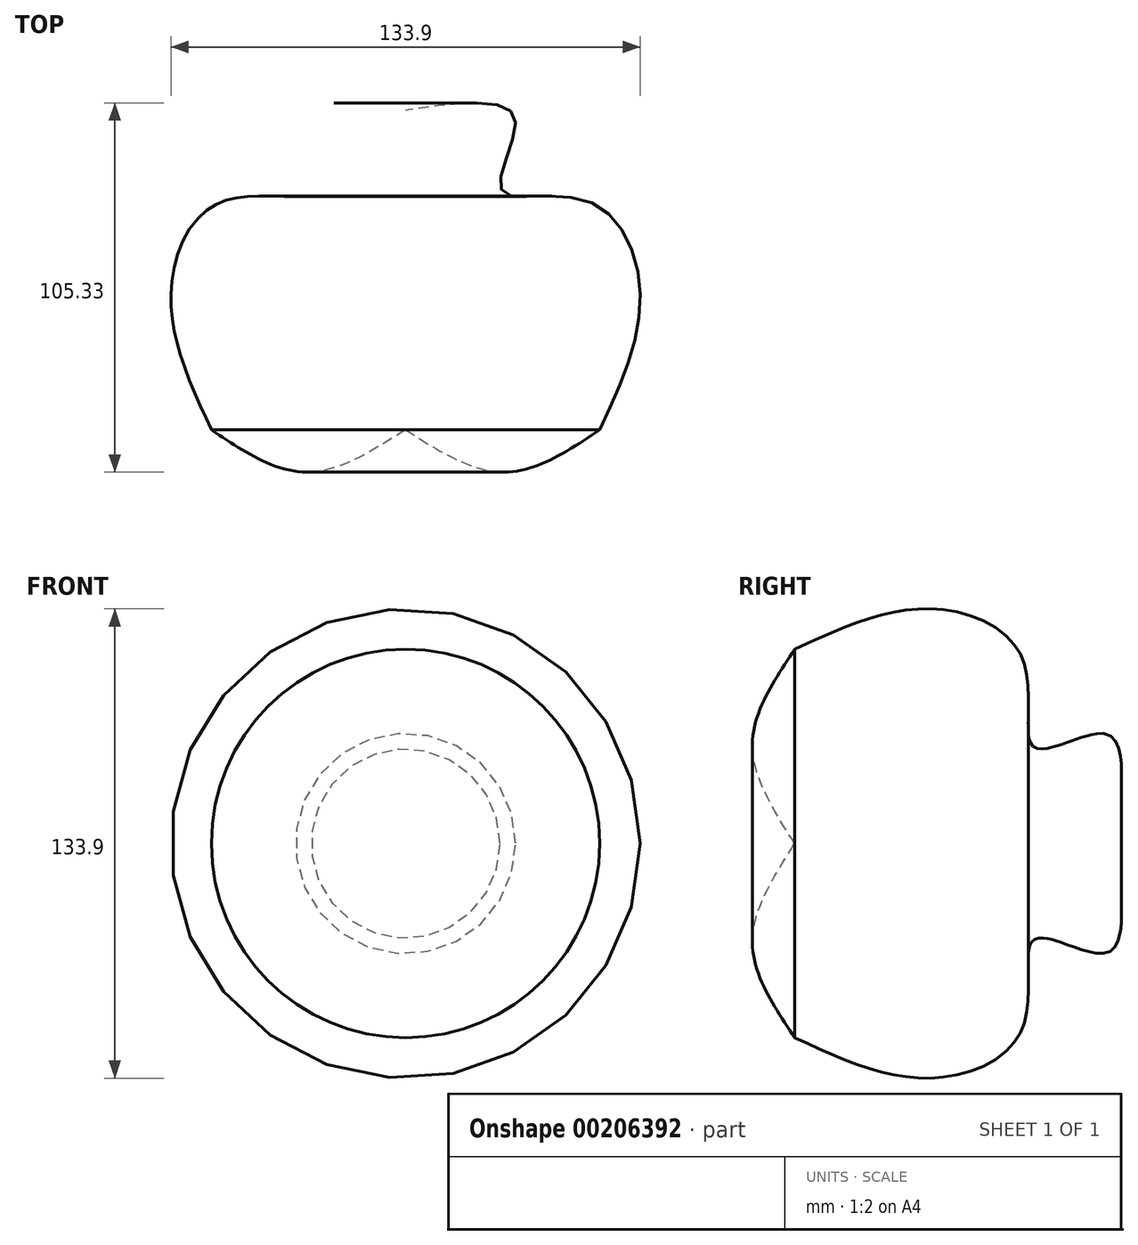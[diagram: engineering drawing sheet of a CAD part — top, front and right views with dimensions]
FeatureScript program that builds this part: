
annotation { "Feature Type Name" : "Feature", "Feature Type Description" : "" }
export const myFeature = defineFeature(function(context is Context, id is Id, definition is map)
    precondition{}
    {
        {
            var Q0;
            Q0=qCreatedBy(makeId("Top.planeOp"),FACE);
            var sketch = newSketch(context, id + "F0", { "sketchPlane" : qUnion([Q0])});
            skLineSegment(sketch, "E0", {"start": v(0, 52.17) * mm, "end": v(0, -38.95) * mm});
            skFitSpline(sketch, "E1", {"points": [v(0, -38.95) * mm, v(28.4, -51.04) * mm, v(55.4, -38.95) * mm], "startDerivative": vector(56.62, -36.15) * mm, "endDerivative": vector(54.17, 36.41) * mm});
            skFitSpline(sketch, "E2", {"points": [v(55.4, -38.95) * mm, v(66.93, 0) * mm, v(51.18, 26.58) * mm, v(27.28, 29.67) * mm, v(31.22, 49.92) * mm, v(0, 52.17) * mm], "startDerivative": vector(75.85, 163.2) * mm, "endDerivative": vector(-213.59, -30.91) * mm});
            skSolve(sketch);
        }
        {
            var Q0;
            Q0=makeQuery(id+"F0.imprint","IMPRINT",FACE,{"disambiguationData":[TD([[makeQuery(id+"F0.imprint","IMPRINT",EDGE,{"derivedFrom":sQuery(id+"F0.wireOp",EDGE,"E0")}),1.0]])]});
            var Q1;
            Q1=sQuery(id+"F0.wireOp",EDGE,"E0");
            revolve(context, id + "F1", {"entities" : qUnion([Q0]), "axis" : qUnion([Q1]), "revolveType" : RevolveType.FULL});
        }
    });
